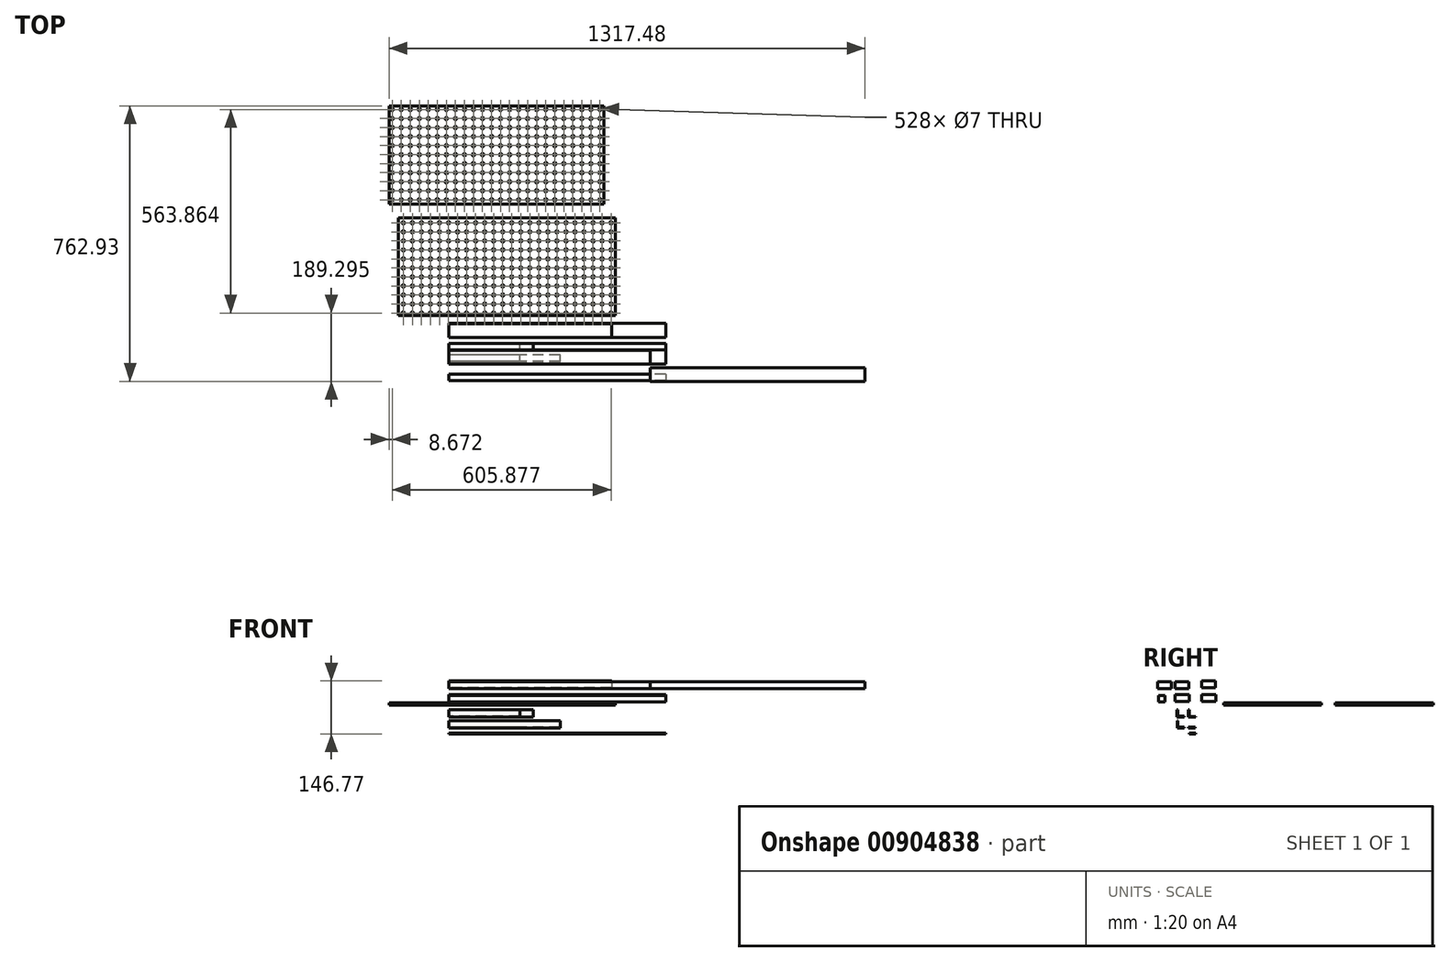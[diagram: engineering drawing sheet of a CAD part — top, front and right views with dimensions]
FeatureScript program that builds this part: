
annotation { "Feature Type Name" : "Feature", "Feature Type Description" : "" }
export const myFeature = defineFeature(function(context is Context, id is Id, definition is map)
    precondition{}
    {
        {
            var Q0;
            Q0=qCreatedBy(makeId("Right.planeOp"),FACE);
            var sketch = newSketch(context, id + "F0", { "sketchPlane" : qUnion([Q0])});
            skLineSegment(sketch, "E0.bottom", {"start": v(-24.33, 9.4) * mm, "end": v(-64.33, 9.4) * mm});
            skLineSegment(sketch, "E0.top", {"start": v(-24.33, 29.4) * mm, "end": v(-64.33, 29.4) * mm});
            skLineSegment(sketch, "E0.left", {"start": v(-24.33, 9.4) * mm, "end": v(-24.33, 29.4) * mm});
            skLineSegment(sketch, "E0.right", {"start": v(-64.33, 9.4) * mm, "end": v(-64.33, 29.4) * mm});
            skPoint(sketch, "E0.middle", {"position": v(-44.33, 19.4) * mm});
            skSolve(sketch);
        }
        {
            var Q0;
            Q0=qCreatedBy(makeId("Right.planeOp"),FACE);
            var sketch = newSketch(context, id + "F1", { "sketchPlane" : qUnion([Q0])});
            skLineSegment(sketch, "E1.bottom", {"start": v(49.06, 9.14) * mm, "end": v(9.06, 9.14) * mm});
            skLineSegment(sketch, "E1.top", {"start": v(49.06, 29.14) * mm, "end": v(9.06, 29.14) * mm});
            skLineSegment(sketch, "E1.left", {"start": v(49.06, 9.14) * mm, "end": v(49.06, 29.14) * mm});
            skLineSegment(sketch, "E1.right", {"start": v(9.06, 9.14) * mm, "end": v(9.06, 29.14) * mm});
            skPoint(sketch, "E1.middle", {"position": v(29.06, 19.14) * mm});
            skSolve(sketch);
        }
        {
            var Q0;
            Q0=qCreatedBy(makeId("Right.planeOp"),FACE);
            var sketch = newSketch(context, id + "F2", { "sketchPlane" : qUnion([Q0])});
            skLineSegment(sketch, "E2", {"start": v(-58.64, -13.36) * mm, "end": v(-58.64, -33.36) * mm});
            skLineSegment(sketch, "E3", {"start": v(-58.64, -33.36) * mm, "end": v(-38.64, -33.36) * mm});
            skLineSegment(sketch, "E4.0", {"start": v(-56.64, -31.36) * mm, "end": v(-38.64, -31.36) * mm});
            skLineSegment(sketch, "E4.1", {"start": v(-56.64, -13.36) * mm, "end": v(-56.64, -31.36) * mm});
            skLineSegment(sketch, "E5", {"start": v(-58.64, -13.36) * mm, "end": v(-56.64, -13.36) * mm});
            skLineSegment(sketch, "E6", {"start": v(-38.64, -31.36) * mm, "end": v(-38.64, -33.36) * mm});
            skSolve(sketch);
        }
        {
            var Q0;
            Q0=qCreatedBy(makeId("Right.planeOp"),FACE);
            var sketch = newSketch(context, id + "F3", { "sketchPlane" : qUnion([Q0])});
            skLineSegment(sketch, "E7.bottom", {"start": v(-91.9, 7.9) * mm, "end": v(-109.9, 7.9) * mm});
            skLineSegment(sketch, "E7.top", {"start": v(-91.9, 25.9) * mm, "end": v(-109.9, 25.9) * mm});
            skLineSegment(sketch, "E7.left", {"start": v(-91.9, 7.9) * mm, "end": v(-91.9, 25.9) * mm});
            skLineSegment(sketch, "E7.right", {"start": v(-109.9, 7.9) * mm, "end": v(-109.9, 25.9) * mm});
            skPoint(sketch, "E7.middle", {"position": v(-100.9, 16.9) * mm});
            skSolve(sketch);
        }
        {
            var Q0;
            Q0=makeQuery(id+"F2.imprint","IMPRINT",FACE,{"disambiguationData":[TD([[makeQuery(id+"F2.imprint","IMPRINT",EDGE,{"derivedFrom":sQuery(id+"F2.wireOp",EDGE,"E2")}),1.0]])]});
            extrude(context, id + "F4", {"entities" : qUnion([Q0]), "depth" : 196.11 * mm, "offsetDistance" : 25.4 * mm});
        }
        {
            var Q0;
            Q0=makeQuery(id+"F1.imprint","IMPRINT",FACE,{"disambiguationData":[TD([[makeQuery(id+"F1.imprint","IMPRINT",EDGE,{"derivedFrom":sQuery(id+"F1.wireOp",EDGE,"E1.bottom")}),-1.0]])]});
            extrude(context, id + "F5", {"entities" : qUnion([Q0]), "depth" : 600 * mm, "offsetDistance" : 25.4 * mm});
        }
        {
            var Q0;
            Q0=makeQuery(id+"F0.imprint","IMPRINT",FACE,{"disambiguationData":[TD([[makeQuery(id+"F0.imprint","IMPRINT",EDGE,{"derivedFrom":sQuery(id+"F0.wireOp",EDGE,"E0.bottom")}),-1.0]])]});
            extrude(context, id + "F6", {"entities" : qUnion([Q0]), "depth" : 600 * mm, "offsetDistance" : 25.4 * mm});
        }
        {
            var Q0;
            Q0=makeQuery(id+"F3.imprint","IMPRINT",FACE,{"disambiguationData":[TD([[makeQuery(id+"F3.imprint","IMPRINT",EDGE,{"derivedFrom":sQuery(id+"F3.wireOp",EDGE,"E7.bottom")}),-1.0]])]});
            extrude(context, id + "F7", {"entities" : qUnion([Q0]), "depth" : 600 * mm, "offsetDistance" : 25.4 * mm});
        }
        {
            var Q0;
            Q0=qCreatedBy(makeId("Right.planeOp"),FACE);
            var sketch = newSketch(context, id + "F8", { "sketchPlane" : qUnion([Q0])});
            skLineSegment(sketch, "E8", {"start": v(-58.2, -43.86) * mm, "end": v(-58.2, -63.86) * mm});
            skLineSegment(sketch, "E9", {"start": v(-58.2, -63.86) * mm, "end": v(-38.2, -63.86) * mm});
            skLineSegment(sketch, "E10.0", {"start": v(-56.2, -61.86) * mm, "end": v(-38.2, -61.86) * mm});
            skLineSegment(sketch, "E10.1", {"start": v(-56.2, -43.86) * mm, "end": v(-56.2, -61.86) * mm});
            skLineSegment(sketch, "E11", {"start": v(-58.2, -43.86) * mm, "end": v(-56.2, -43.86) * mm});
            skLineSegment(sketch, "E12", {"start": v(-38.2, -61.86) * mm, "end": v(-38.2, -63.86) * mm});
            skSolve(sketch);
        }
        {
            var Q0;
            Q0=qSketchRegion(id+"F8",true);
            extrude(context, id + "F9", {"entities" : qUnion([Q0]), "depth" : 308 * mm, "offsetDistance" : 25.4 * mm});
        }
        {
            var Q0;
            Q0=qCreatedBy(makeId("Right.planeOp"),FACE);
            var sketch = newSketch(context, id + "F10", { "sketchPlane" : qUnion([Q0])});
            skLineSegment(sketch, "E13", {"start": v(-26.75, -13.52) * mm, "end": v(-26.75, -33.52) * mm});
            skLineSegment(sketch, "E14", {"start": v(-26.75, -33.52) * mm, "end": v(-6.75, -33.52) * mm});
            skLineSegment(sketch, "E15.0", {"start": v(-24.75, -31.52) * mm, "end": v(-6.75, -31.52) * mm});
            skLineSegment(sketch, "E15.1", {"start": v(-24.75, -13.52) * mm, "end": v(-24.75, -31.52) * mm});
            skLineSegment(sketch, "E16", {"start": v(-26.75, -13.52) * mm, "end": v(-24.75, -13.52) * mm});
            skLineSegment(sketch, "E17", {"start": v(-6.75, -31.52) * mm, "end": v(-6.75, -33.52) * mm});
            skSolve(sketch);
        }
        {
            var Q0;
            Q0=qSketchRegion(id+"F10",true);
            extrude(context, id + "F11", {"entities" : qUnion([Q0]), "depth" : 234 * mm, "offsetDistance" : 25 * mm});
        }
        {
            var Q0;
            Q0=qCreatedBy(makeId("Top.planeOp"),FACE);
            var sketch = newSketch(context, id + "F12", { "sketchPlane" : qUnion([Q0])});
            skLineSegment(sketch, "E18.bottom", {"start": v(-139.49, 340.67) * mm, "end": v(460.51, 340.67) * mm});
            skLineSegment(sketch, "E18.top", {"start": v(-139.49, 70.67) * mm, "end": v(460.51, 70.67) * mm});
            skLineSegment(sketch, "E18.left", {"start": v(-139.49, 340.67) * mm, "end": v(-139.49, 70.67) * mm});
            skLineSegment(sketch, "E18.right", {"start": v(460.51, 340.67) * mm, "end": v(460.51, 70.67) * mm});
            skCircle(sketch, "E19", {"center": v(-126.03, 327.27) * mm, "radius": 3.5 * mm});
            skCircle(sketch, "E20.0.1.0", {"center": v(-126.03, 302.27) * mm, "radius": 3.5 * mm});
            skCircle(sketch, "E20.0.2.0", {"center": v(-126.03, 277.27) * mm, "radius": 3.5 * mm});
            skCircle(sketch, "E20.0.3.0", {"center": v(-126.03, 252.27) * mm, "radius": 3.5 * mm});
            skCircle(sketch, "E20.0.4.0", {"center": v(-126.03, 227.27) * mm, "radius": 3.5 * mm});
            skCircle(sketch, "E20.0.5.0", {"center": v(-126.03, 202.27) * mm, "radius": 3.5 * mm});
            skCircle(sketch, "E20.0.6.0", {"center": v(-126.03, 177.27) * mm, "radius": 3.5 * mm});
            skCircle(sketch, "E20.0.7.0", {"center": v(-126.03, 152.27) * mm, "radius": 3.5 * mm});
            skCircle(sketch, "E20.0.8.0", {"center": v(-126.03, 127.27) * mm, "radius": 3.5 * mm});
            skCircle(sketch, "E20.0.9.0", {"center": v(-126.03, 102.27) * mm, "radius": 3.5 * mm});
            skCircle(sketch, "E20.0.10.0", {"center": v(-126.03, 77.27) * mm, "radius": 3.5 * mm});
            skCircle(sketch, "E20.1.0.0", {"center": v(-101.03, 327.27) * mm, "radius": 3.5 * mm});
            skCircle(sketch, "E20.1.1.0", {"center": v(-101.03, 302.27) * mm, "radius": 3.5 * mm});
            skCircle(sketch, "E20.1.2.0", {"center": v(-101.03, 277.27) * mm, "radius": 3.5 * mm});
            skCircle(sketch, "E20.1.3.0", {"center": v(-101.03, 252.27) * mm, "radius": 3.5 * mm});
            skCircle(sketch, "E20.1.4.0", {"center": v(-101.03, 227.27) * mm, "radius": 3.5 * mm});
            skCircle(sketch, "E20.1.5.0", {"center": v(-101.03, 202.27) * mm, "radius": 3.5 * mm});
            skCircle(sketch, "E20.1.6.0", {"center": v(-101.03, 177.27) * mm, "radius": 3.5 * mm});
            skCircle(sketch, "E20.1.7.0", {"center": v(-101.03, 152.27) * mm, "radius": 3.5 * mm});
            skCircle(sketch, "E20.1.8.0", {"center": v(-101.03, 127.27) * mm, "radius": 3.5 * mm});
            skCircle(sketch, "E20.1.9.0", {"center": v(-101.03, 102.27) * mm, "radius": 3.5 * mm});
            skCircle(sketch, "E20.1.10.0", {"center": v(-101.03, 77.27) * mm, "radius": 3.5 * mm});
            skCircle(sketch, "E20.2.0.0", {"center": v(-76.03, 327.27) * mm, "radius": 3.5 * mm});
            skCircle(sketch, "E20.2.1.0", {"center": v(-76.03, 302.27) * mm, "radius": 3.5 * mm});
            skCircle(sketch, "E20.2.2.0", {"center": v(-76.03, 277.27) * mm, "radius": 3.5 * mm});
            skCircle(sketch, "E20.2.3.0", {"center": v(-76.03, 252.27) * mm, "radius": 3.5 * mm});
            skCircle(sketch, "E20.2.4.0", {"center": v(-76.03, 227.27) * mm, "radius": 3.5 * mm});
            skCircle(sketch, "E20.2.5.0", {"center": v(-76.03, 202.27) * mm, "radius": 3.5 * mm});
            skCircle(sketch, "E20.2.6.0", {"center": v(-76.03, 177.27) * mm, "radius": 3.5 * mm});
            skCircle(sketch, "E20.2.7.0", {"center": v(-76.03, 152.27) * mm, "radius": 3.5 * mm});
            skCircle(sketch, "E20.2.8.0", {"center": v(-76.03, 127.27) * mm, "radius": 3.5 * mm});
            skCircle(sketch, "E20.2.9.0", {"center": v(-76.03, 102.27) * mm, "radius": 3.5 * mm});
            skCircle(sketch, "E20.2.10.0", {"center": v(-76.03, 77.27) * mm, "radius": 3.5 * mm});
            skCircle(sketch, "E20.3.0.0", {"center": v(-51.03, 327.27) * mm, "radius": 3.5 * mm});
            skCircle(sketch, "E20.3.1.0", {"center": v(-51.03, 302.27) * mm, "radius": 3.5 * mm});
            skCircle(sketch, "E20.3.2.0", {"center": v(-51.03, 277.27) * mm, "radius": 3.5 * mm});
            skCircle(sketch, "E20.3.3.0", {"center": v(-51.03, 252.27) * mm, "radius": 3.5 * mm});
            skCircle(sketch, "E20.3.4.0", {"center": v(-51.03, 227.27) * mm, "radius": 3.5 * mm});
            skCircle(sketch, "E20.3.5.0", {"center": v(-51.03, 202.27) * mm, "radius": 3.5 * mm});
            skCircle(sketch, "E20.3.6.0", {"center": v(-51.03, 177.27) * mm, "radius": 3.5 * mm});
            skCircle(sketch, "E20.3.7.0", {"center": v(-51.03, 152.27) * mm, "radius": 3.5 * mm});
            skCircle(sketch, "E20.3.8.0", {"center": v(-51.03, 127.27) * mm, "radius": 3.5 * mm});
            skCircle(sketch, "E20.3.9.0", {"center": v(-51.03, 102.27) * mm, "radius": 3.5 * mm});
            skCircle(sketch, "E20.3.10.0", {"center": v(-51.03, 77.27) * mm, "radius": 3.5 * mm});
            skCircle(sketch, "E20.4.0.0", {"center": v(-26.03, 327.27) * mm, "radius": 3.5 * mm});
            skCircle(sketch, "E20.4.1.0", {"center": v(-26.03, 302.27) * mm, "radius": 3.5 * mm});
            skCircle(sketch, "E20.4.2.0", {"center": v(-26.03, 277.27) * mm, "radius": 3.5 * mm});
            skCircle(sketch, "E20.4.3.0", {"center": v(-26.03, 252.27) * mm, "radius": 3.5 * mm});
            skCircle(sketch, "E20.4.4.0", {"center": v(-26.03, 227.27) * mm, "radius": 3.5 * mm});
            skCircle(sketch, "E20.4.5.0", {"center": v(-26.03, 202.27) * mm, "radius": 3.5 * mm});
            skCircle(sketch, "E20.4.6.0", {"center": v(-26.03, 177.27) * mm, "radius": 3.5 * mm});
            skCircle(sketch, "E20.4.7.0", {"center": v(-26.03, 152.27) * mm, "radius": 3.5 * mm});
            skCircle(sketch, "E20.4.8.0", {"center": v(-26.03, 127.27) * mm, "radius": 3.5 * mm});
            skCircle(sketch, "E20.4.9.0", {"center": v(-26.03, 102.27) * mm, "radius": 3.5 * mm});
            skCircle(sketch, "E20.4.10.0", {"center": v(-26.03, 77.27) * mm, "radius": 3.5 * mm});
            skCircle(sketch, "E20.5.0.0", {"center": v(-1.03, 327.27) * mm, "radius": 3.5 * mm});
            skCircle(sketch, "E20.5.1.0", {"center": v(-1.03, 302.27) * mm, "radius": 3.5 * mm});
            skCircle(sketch, "E20.5.2.0", {"center": v(-1.03, 277.27) * mm, "radius": 3.5 * mm});
            skCircle(sketch, "E20.5.3.0", {"center": v(-1.03, 252.27) * mm, "radius": 3.5 * mm});
            skCircle(sketch, "E20.5.4.0", {"center": v(-1.03, 227.27) * mm, "radius": 3.5 * mm});
            skCircle(sketch, "E20.5.5.0", {"center": v(-1.03, 202.27) * mm, "radius": 3.5 * mm});
            skCircle(sketch, "E20.5.6.0", {"center": v(-1.03, 177.27) * mm, "radius": 3.5 * mm});
            skCircle(sketch, "E20.5.7.0", {"center": v(-1.03, 152.27) * mm, "radius": 3.5 * mm});
            skCircle(sketch, "E20.5.8.0", {"center": v(-1.03, 127.27) * mm, "radius": 3.5 * mm});
            skCircle(sketch, "E20.5.9.0", {"center": v(-1.03, 102.27) * mm, "radius": 3.5 * mm});
            skCircle(sketch, "E20.5.10.0", {"center": v(-1.03, 77.27) * mm, "radius": 3.5 * mm});
            skCircle(sketch, "E20.6.0.0", {"center": v(23.97, 327.27) * mm, "radius": 3.5 * mm});
            skCircle(sketch, "E20.6.1.0", {"center": v(23.97, 302.27) * mm, "radius": 3.5 * mm});
            skCircle(sketch, "E20.6.2.0", {"center": v(23.97, 277.27) * mm, "radius": 3.5 * mm});
            skCircle(sketch, "E20.6.3.0", {"center": v(23.97, 252.27) * mm, "radius": 3.5 * mm});
            skCircle(sketch, "E20.6.4.0", {"center": v(23.97, 227.27) * mm, "radius": 3.5 * mm});
            skCircle(sketch, "E20.6.5.0", {"center": v(23.97, 202.27) * mm, "radius": 3.5 * mm});
            skCircle(sketch, "E20.6.6.0", {"center": v(23.97, 177.27) * mm, "radius": 3.5 * mm});
            skCircle(sketch, "E20.6.7.0", {"center": v(23.97, 152.27) * mm, "radius": 3.5 * mm});
            skCircle(sketch, "E20.6.8.0", {"center": v(23.97, 127.27) * mm, "radius": 3.5 * mm});
            skCircle(sketch, "E20.6.9.0", {"center": v(23.97, 102.27) * mm, "radius": 3.5 * mm});
            skCircle(sketch, "E20.6.10.0", {"center": v(23.97, 77.27) * mm, "radius": 3.5 * mm});
            skCircle(sketch, "E20.7.0.0", {"center": v(48.97, 327.27) * mm, "radius": 3.5 * mm});
            skCircle(sketch, "E20.7.1.0", {"center": v(48.97, 302.27) * mm, "radius": 3.5 * mm});
            skCircle(sketch, "E20.7.2.0", {"center": v(48.97, 277.27) * mm, "radius": 3.5 * mm});
            skCircle(sketch, "E20.7.3.0", {"center": v(48.97, 252.27) * mm, "radius": 3.5 * mm});
            skCircle(sketch, "E20.7.4.0", {"center": v(48.97, 227.27) * mm, "radius": 3.5 * mm});
            skCircle(sketch, "E20.7.5.0", {"center": v(48.97, 202.27) * mm, "radius": 3.5 * mm});
            skCircle(sketch, "E20.7.6.0", {"center": v(48.97, 177.27) * mm, "radius": 3.5 * mm});
            skCircle(sketch, "E20.7.7.0", {"center": v(48.97, 152.27) * mm, "radius": 3.5 * mm});
            skCircle(sketch, "E20.7.8.0", {"center": v(48.97, 127.27) * mm, "radius": 3.5 * mm});
            skCircle(sketch, "E20.7.9.0", {"center": v(48.97, 102.27) * mm, "radius": 3.5 * mm});
            skCircle(sketch, "E20.7.10.0", {"center": v(48.97, 77.27) * mm, "radius": 3.5 * mm});
            skCircle(sketch, "E20.8.0.0", {"center": v(73.97, 327.27) * mm, "radius": 3.5 * mm});
            skCircle(sketch, "E20.8.1.0", {"center": v(73.97, 302.27) * mm, "radius": 3.5 * mm});
            skCircle(sketch, "E20.8.2.0", {"center": v(73.97, 277.27) * mm, "radius": 3.5 * mm});
            skCircle(sketch, "E20.8.3.0", {"center": v(73.97, 252.27) * mm, "radius": 3.5 * mm});
            skCircle(sketch, "E20.8.4.0", {"center": v(73.97, 227.27) * mm, "radius": 3.5 * mm});
            skCircle(sketch, "E20.8.5.0", {"center": v(73.97, 202.27) * mm, "radius": 3.5 * mm});
            skCircle(sketch, "E20.8.6.0", {"center": v(73.97, 177.27) * mm, "radius": 3.5 * mm});
            skCircle(sketch, "E20.8.7.0", {"center": v(73.97, 152.27) * mm, "radius": 3.5 * mm});
            skCircle(sketch, "E20.8.8.0", {"center": v(73.97, 127.27) * mm, "radius": 3.5 * mm});
            skCircle(sketch, "E20.8.9.0", {"center": v(73.97, 102.27) * mm, "radius": 3.5 * mm});
            skCircle(sketch, "E20.8.10.0", {"center": v(73.97, 77.27) * mm, "radius": 3.5 * mm});
            skCircle(sketch, "E20.9.0.0", {"center": v(98.97, 327.27) * mm, "radius": 3.5 * mm});
            skCircle(sketch, "E20.9.1.0", {"center": v(98.97, 302.27) * mm, "radius": 3.5 * mm});
            skCircle(sketch, "E20.9.2.0", {"center": v(98.97, 277.27) * mm, "radius": 3.5 * mm});
            skCircle(sketch, "E20.9.3.0", {"center": v(98.97, 252.27) * mm, "radius": 3.5 * mm});
            skCircle(sketch, "E20.9.4.0", {"center": v(98.97, 227.27) * mm, "radius": 3.5 * mm});
            skCircle(sketch, "E20.9.5.0", {"center": v(98.97, 202.27) * mm, "radius": 3.5 * mm});
            skCircle(sketch, "E20.9.6.0", {"center": v(98.97, 177.27) * mm, "radius": 3.5 * mm});
            skCircle(sketch, "E20.9.7.0", {"center": v(98.97, 152.27) * mm, "radius": 3.5 * mm});
            skCircle(sketch, "E20.9.8.0", {"center": v(98.97, 127.27) * mm, "radius": 3.5 * mm});
            skCircle(sketch, "E20.9.9.0", {"center": v(98.97, 102.27) * mm, "radius": 3.5 * mm});
            skCircle(sketch, "E20.9.10.0", {"center": v(98.97, 77.27) * mm, "radius": 3.5 * mm});
            skCircle(sketch, "E20.10.0.0", {"center": v(123.97, 327.27) * mm, "radius": 3.5 * mm});
            skCircle(sketch, "E20.10.1.0", {"center": v(123.97, 302.27) * mm, "radius": 3.5 * mm});
            skCircle(sketch, "E20.10.2.0", {"center": v(123.97, 277.27) * mm, "radius": 3.5 * mm});
            skCircle(sketch, "E20.10.3.0", {"center": v(123.97, 252.27) * mm, "radius": 3.5 * mm});
            skCircle(sketch, "E20.10.4.0", {"center": v(123.97, 227.27) * mm, "radius": 3.5 * mm});
            skCircle(sketch, "E20.10.5.0", {"center": v(123.97, 202.27) * mm, "radius": 3.5 * mm});
            skCircle(sketch, "E20.10.6.0", {"center": v(123.97, 177.27) * mm, "radius": 3.5 * mm});
            skCircle(sketch, "E20.10.7.0", {"center": v(123.97, 152.27) * mm, "radius": 3.5 * mm});
            skCircle(sketch, "E20.10.8.0", {"center": v(123.97, 127.27) * mm, "radius": 3.5 * mm});
            skCircle(sketch, "E20.10.9.0", {"center": v(123.97, 102.27) * mm, "radius": 3.5 * mm});
            skCircle(sketch, "E20.10.10.0", {"center": v(123.97, 77.27) * mm, "radius": 3.5 * mm});
            skCircle(sketch, "E20.11.0.0", {"center": v(148.97, 327.27) * mm, "radius": 3.5 * mm});
            skCircle(sketch, "E20.11.1.0", {"center": v(148.97, 302.27) * mm, "radius": 3.5 * mm});
            skCircle(sketch, "E20.11.2.0", {"center": v(148.97, 277.27) * mm, "radius": 3.5 * mm});
            skCircle(sketch, "E20.11.3.0", {"center": v(148.97, 252.27) * mm, "radius": 3.5 * mm});
            skCircle(sketch, "E20.11.4.0", {"center": v(148.97, 227.27) * mm, "radius": 3.5 * mm});
            skCircle(sketch, "E20.11.5.0", {"center": v(148.97, 202.27) * mm, "radius": 3.5 * mm});
            skCircle(sketch, "E20.11.6.0", {"center": v(148.97, 177.27) * mm, "radius": 3.5 * mm});
            skCircle(sketch, "E20.11.7.0", {"center": v(148.97, 152.27) * mm, "radius": 3.5 * mm});
            skCircle(sketch, "E20.11.8.0", {"center": v(148.97, 127.27) * mm, "radius": 3.5 * mm});
            skCircle(sketch, "E20.11.9.0", {"center": v(148.97, 102.27) * mm, "radius": 3.5 * mm});
            skCircle(sketch, "E20.11.10.0", {"center": v(148.97, 77.27) * mm, "radius": 3.5 * mm});
            skCircle(sketch, "E20.12.0.0", {"center": v(173.97, 327.27) * mm, "radius": 3.5 * mm});
            skCircle(sketch, "E20.12.1.0", {"center": v(173.97, 302.27) * mm, "radius": 3.5 * mm});
            skCircle(sketch, "E20.12.2.0", {"center": v(173.97, 277.27) * mm, "radius": 3.5 * mm});
            skCircle(sketch, "E20.12.3.0", {"center": v(173.97, 252.27) * mm, "radius": 3.5 * mm});
            skCircle(sketch, "E20.12.4.0", {"center": v(173.97, 227.27) * mm, "radius": 3.5 * mm});
            skCircle(sketch, "E20.12.5.0", {"center": v(173.97, 202.27) * mm, "radius": 3.5 * mm});
            skCircle(sketch, "E20.12.6.0", {"center": v(173.97, 177.27) * mm, "radius": 3.5 * mm});
            skCircle(sketch, "E20.12.7.0", {"center": v(173.97, 152.27) * mm, "radius": 3.5 * mm});
            skCircle(sketch, "E20.12.8.0", {"center": v(173.97, 127.27) * mm, "radius": 3.5 * mm});
            skCircle(sketch, "E20.12.9.0", {"center": v(173.97, 102.27) * mm, "radius": 3.5 * mm});
            skCircle(sketch, "E20.12.10.0", {"center": v(173.97, 77.27) * mm, "radius": 3.5 * mm});
            skCircle(sketch, "E20.13.0.0", {"center": v(198.97, 327.27) * mm, "radius": 3.5 * mm});
            skCircle(sketch, "E20.13.1.0", {"center": v(198.97, 302.27) * mm, "radius": 3.5 * mm});
            skCircle(sketch, "E20.13.2.0", {"center": v(198.97, 277.27) * mm, "radius": 3.5 * mm});
            skCircle(sketch, "E20.13.3.0", {"center": v(198.97, 252.27) * mm, "radius": 3.5 * mm});
            skCircle(sketch, "E20.13.4.0", {"center": v(198.97, 227.27) * mm, "radius": 3.5 * mm});
            skCircle(sketch, "E20.13.5.0", {"center": v(198.97, 202.27) * mm, "radius": 3.5 * mm});
            skCircle(sketch, "E20.13.6.0", {"center": v(198.97, 177.27) * mm, "radius": 3.5 * mm});
            skCircle(sketch, "E20.13.7.0", {"center": v(198.97, 152.27) * mm, "radius": 3.5 * mm});
            skCircle(sketch, "E20.13.8.0", {"center": v(198.97, 127.27) * mm, "radius": 3.5 * mm});
            skCircle(sketch, "E20.13.9.0", {"center": v(198.97, 102.27) * mm, "radius": 3.5 * mm});
            skCircle(sketch, "E20.13.10.0", {"center": v(198.97, 77.27) * mm, "radius": 3.5 * mm});
            skCircle(sketch, "E20.14.0.0", {"center": v(223.97, 327.27) * mm, "radius": 3.5 * mm});
            skCircle(sketch, "E20.14.1.0", {"center": v(223.97, 302.27) * mm, "radius": 3.5 * mm});
            skCircle(sketch, "E20.14.2.0", {"center": v(223.97, 277.27) * mm, "radius": 3.5 * mm});
            skCircle(sketch, "E20.14.3.0", {"center": v(223.97, 252.27) * mm, "radius": 3.5 * mm});
            skCircle(sketch, "E20.14.4.0", {"center": v(223.97, 227.27) * mm, "radius": 3.5 * mm});
            skCircle(sketch, "E20.14.5.0", {"center": v(223.97, 202.27) * mm, "radius": 3.5 * mm});
            skCircle(sketch, "E20.14.6.0", {"center": v(223.97, 177.27) * mm, "radius": 3.5 * mm});
            skCircle(sketch, "E20.14.7.0", {"center": v(223.97, 152.27) * mm, "radius": 3.5 * mm});
            skCircle(sketch, "E20.14.8.0", {"center": v(223.97, 127.27) * mm, "radius": 3.5 * mm});
            skCircle(sketch, "E20.14.9.0", {"center": v(223.97, 102.27) * mm, "radius": 3.5 * mm});
            skCircle(sketch, "E20.14.10.0", {"center": v(223.97, 77.27) * mm, "radius": 3.5 * mm});
            skCircle(sketch, "E20.15.0.0", {"center": v(248.97, 327.27) * mm, "radius": 3.5 * mm});
            skCircle(sketch, "E20.15.1.0", {"center": v(248.97, 302.27) * mm, "radius": 3.5 * mm});
            skCircle(sketch, "E20.15.2.0", {"center": v(248.97, 277.27) * mm, "radius": 3.5 * mm});
            skCircle(sketch, "E20.15.3.0", {"center": v(248.97, 252.27) * mm, "radius": 3.5 * mm});
            skCircle(sketch, "E20.15.4.0", {"center": v(248.97, 227.27) * mm, "radius": 3.5 * mm});
            skCircle(sketch, "E20.15.5.0", {"center": v(248.97, 202.27) * mm, "radius": 3.5 * mm});
            skCircle(sketch, "E20.15.6.0", {"center": v(248.97, 177.27) * mm, "radius": 3.5 * mm});
            skCircle(sketch, "E20.15.7.0", {"center": v(248.97, 152.27) * mm, "radius": 3.5 * mm});
            skCircle(sketch, "E20.15.8.0", {"center": v(248.97, 127.27) * mm, "radius": 3.5 * mm});
            skCircle(sketch, "E20.15.9.0", {"center": v(248.97, 102.27) * mm, "radius": 3.5 * mm});
            skCircle(sketch, "E20.15.10.0", {"center": v(248.97, 77.27) * mm, "radius": 3.5 * mm});
            skCircle(sketch, "E20.16.0.0", {"center": v(273.97, 327.27) * mm, "radius": 3.5 * mm});
            skCircle(sketch, "E20.16.1.0", {"center": v(273.97, 302.27) * mm, "radius": 3.5 * mm});
            skCircle(sketch, "E20.16.2.0", {"center": v(273.97, 277.27) * mm, "radius": 3.5 * mm});
            skCircle(sketch, "E20.16.3.0", {"center": v(273.97, 252.27) * mm, "radius": 3.5 * mm});
            skCircle(sketch, "E20.16.4.0", {"center": v(273.97, 227.27) * mm, "radius": 3.5 * mm});
            skCircle(sketch, "E20.16.5.0", {"center": v(273.97, 202.27) * mm, "radius": 3.5 * mm});
            skCircle(sketch, "E20.16.6.0", {"center": v(273.97, 177.27) * mm, "radius": 3.5 * mm});
            skCircle(sketch, "E20.16.7.0", {"center": v(273.97, 152.27) * mm, "radius": 3.5 * mm});
            skCircle(sketch, "E20.16.8.0", {"center": v(273.97, 127.27) * mm, "radius": 3.5 * mm});
            skCircle(sketch, "E20.16.9.0", {"center": v(273.97, 102.27) * mm, "radius": 3.5 * mm});
            skCircle(sketch, "E20.16.10.0", {"center": v(273.97, 77.27) * mm, "radius": 3.5 * mm});
            skCircle(sketch, "E20.17.0.0", {"center": v(298.97, 327.27) * mm, "radius": 3.5 * mm});
            skCircle(sketch, "E20.17.1.0", {"center": v(298.97, 302.27) * mm, "radius": 3.5 * mm});
            skCircle(sketch, "E20.17.2.0", {"center": v(298.97, 277.27) * mm, "radius": 3.5 * mm});
            skCircle(sketch, "E20.17.3.0", {"center": v(298.97, 252.27) * mm, "radius": 3.5 * mm});
            skCircle(sketch, "E20.17.4.0", {"center": v(298.97, 227.27) * mm, "radius": 3.5 * mm});
            skCircle(sketch, "E20.17.5.0", {"center": v(298.97, 202.27) * mm, "radius": 3.5 * mm});
            skCircle(sketch, "E20.17.6.0", {"center": v(298.97, 177.27) * mm, "radius": 3.5 * mm});
            skCircle(sketch, "E20.17.7.0", {"center": v(298.97, 152.27) * mm, "radius": 3.5 * mm});
            skCircle(sketch, "E20.17.8.0", {"center": v(298.97, 127.27) * mm, "radius": 3.5 * mm});
            skCircle(sketch, "E20.17.9.0", {"center": v(298.97, 102.27) * mm, "radius": 3.5 * mm});
            skCircle(sketch, "E20.17.10.0", {"center": v(298.97, 77.27) * mm, "radius": 3.5 * mm});
            skCircle(sketch, "E20.18.0.0", {"center": v(323.97, 327.27) * mm, "radius": 3.5 * mm});
            skCircle(sketch, "E20.18.1.0", {"center": v(323.97, 302.27) * mm, "radius": 3.5 * mm});
            skCircle(sketch, "E20.18.2.0", {"center": v(323.97, 277.27) * mm, "radius": 3.5 * mm});
            skCircle(sketch, "E20.18.3.0", {"center": v(323.97, 252.27) * mm, "radius": 3.5 * mm});
            skCircle(sketch, "E20.18.4.0", {"center": v(323.97, 227.27) * mm, "radius": 3.5 * mm});
            skCircle(sketch, "E20.18.5.0", {"center": v(323.97, 202.27) * mm, "radius": 3.5 * mm});
            skCircle(sketch, "E20.18.6.0", {"center": v(323.97, 177.27) * mm, "radius": 3.5 * mm});
            skCircle(sketch, "E20.18.7.0", {"center": v(323.97, 152.27) * mm, "radius": 3.5 * mm});
            skCircle(sketch, "E20.18.8.0", {"center": v(323.97, 127.27) * mm, "radius": 3.5 * mm});
            skCircle(sketch, "E20.18.9.0", {"center": v(323.97, 102.27) * mm, "radius": 3.5 * mm});
            skCircle(sketch, "E20.18.10.0", {"center": v(323.97, 77.27) * mm, "radius": 3.5 * mm});
            skCircle(sketch, "E20.19.0.0", {"center": v(348.97, 327.27) * mm, "radius": 3.5 * mm});
            skCircle(sketch, "E20.19.1.0", {"center": v(348.97, 302.27) * mm, "radius": 3.5 * mm});
            skCircle(sketch, "E20.19.2.0", {"center": v(348.97, 277.27) * mm, "radius": 3.5 * mm});
            skCircle(sketch, "E20.19.3.0", {"center": v(348.97, 252.27) * mm, "radius": 3.5 * mm});
            skCircle(sketch, "E20.19.4.0", {"center": v(348.97, 227.27) * mm, "radius": 3.5 * mm});
            skCircle(sketch, "E20.19.5.0", {"center": v(348.97, 202.27) * mm, "radius": 3.5 * mm});
            skCircle(sketch, "E20.19.6.0", {"center": v(348.97, 177.27) * mm, "radius": 3.5 * mm});
            skCircle(sketch, "E20.19.7.0", {"center": v(348.97, 152.27) * mm, "radius": 3.5 * mm});
            skCircle(sketch, "E20.19.8.0", {"center": v(348.97, 127.27) * mm, "radius": 3.5 * mm});
            skCircle(sketch, "E20.19.9.0", {"center": v(348.97, 102.27) * mm, "radius": 3.5 * mm});
            skCircle(sketch, "E20.19.10.0", {"center": v(348.97, 77.27) * mm, "radius": 3.5 * mm});
            skCircle(sketch, "E20.20.0.0", {"center": v(373.97, 327.27) * mm, "radius": 3.5 * mm});
            skCircle(sketch, "E20.20.1.0", {"center": v(373.97, 302.27) * mm, "radius": 3.5 * mm});
            skCircle(sketch, "E20.20.2.0", {"center": v(373.97, 277.27) * mm, "radius": 3.5 * mm});
            skCircle(sketch, "E20.20.3.0", {"center": v(373.97, 252.27) * mm, "radius": 3.5 * mm});
            skCircle(sketch, "E20.20.4.0", {"center": v(373.97, 227.27) * mm, "radius": 3.5 * mm});
            skCircle(sketch, "E20.20.5.0", {"center": v(373.97, 202.27) * mm, "radius": 3.5 * mm});
            skCircle(sketch, "E20.20.6.0", {"center": v(373.97, 177.27) * mm, "radius": 3.5 * mm});
            skCircle(sketch, "E20.20.7.0", {"center": v(373.97, 152.27) * mm, "radius": 3.5 * mm});
            skCircle(sketch, "E20.20.8.0", {"center": v(373.97, 127.27) * mm, "radius": 3.5 * mm});
            skCircle(sketch, "E20.20.9.0", {"center": v(373.97, 102.27) * mm, "radius": 3.5 * mm});
            skCircle(sketch, "E20.20.10.0", {"center": v(373.97, 77.27) * mm, "radius": 3.5 * mm});
            skCircle(sketch, "E20.21.0.0", {"center": v(398.97, 327.27) * mm, "radius": 3.5 * mm});
            skCircle(sketch, "E20.21.1.0", {"center": v(398.97, 302.27) * mm, "radius": 3.5 * mm});
            skCircle(sketch, "E20.21.2.0", {"center": v(398.97, 277.27) * mm, "radius": 3.5 * mm});
            skCircle(sketch, "E20.21.3.0", {"center": v(398.97, 252.27) * mm, "radius": 3.5 * mm});
            skCircle(sketch, "E20.21.4.0", {"center": v(398.97, 227.27) * mm, "radius": 3.5 * mm});
            skCircle(sketch, "E20.21.5.0", {"center": v(398.97, 202.27) * mm, "radius": 3.5 * mm});
            skCircle(sketch, "E20.21.6.0", {"center": v(398.97, 177.27) * mm, "radius": 3.5 * mm});
            skCircle(sketch, "E20.21.7.0", {"center": v(398.97, 152.27) * mm, "radius": 3.5 * mm});
            skCircle(sketch, "E20.21.8.0", {"center": v(398.97, 127.27) * mm, "radius": 3.5 * mm});
            skCircle(sketch, "E20.21.9.0", {"center": v(398.97, 102.27) * mm, "radius": 3.5 * mm});
            skCircle(sketch, "E20.21.10.0", {"center": v(398.97, 77.27) * mm, "radius": 3.5 * mm});
            skCircle(sketch, "E20.22.0.0", {"center": v(423.97, 327.27) * mm, "radius": 3.5 * mm});
            skCircle(sketch, "E20.22.1.0", {"center": v(423.97, 302.27) * mm, "radius": 3.5 * mm});
            skCircle(sketch, "E20.22.2.0", {"center": v(423.97, 277.27) * mm, "radius": 3.5 * mm});
            skCircle(sketch, "E20.22.3.0", {"center": v(423.97, 252.27) * mm, "radius": 3.5 * mm});
            skCircle(sketch, "E20.22.4.0", {"center": v(423.97, 227.27) * mm, "radius": 3.5 * mm});
            skCircle(sketch, "E20.22.5.0", {"center": v(423.97, 202.27) * mm, "radius": 3.5 * mm});
            skCircle(sketch, "E20.22.6.0", {"center": v(423.97, 177.27) * mm, "radius": 3.5 * mm});
            skCircle(sketch, "E20.22.7.0", {"center": v(423.97, 152.27) * mm, "radius": 3.5 * mm});
            skCircle(sketch, "E20.22.8.0", {"center": v(423.97, 127.27) * mm, "radius": 3.5 * mm});
            skCircle(sketch, "E20.22.9.0", {"center": v(423.97, 102.27) * mm, "radius": 3.5 * mm});
            skCircle(sketch, "E20.22.10.0", {"center": v(423.97, 77.27) * mm, "radius": 3.5 * mm});
            skCircle(sketch, "E20.23.0.0", {"center": v(448.97, 327.27) * mm, "radius": 3.5 * mm});
            skCircle(sketch, "E20.23.1.0", {"center": v(448.97, 302.27) * mm, "radius": 3.5 * mm});
            skCircle(sketch, "E20.23.2.0", {"center": v(448.97, 277.27) * mm, "radius": 3.5 * mm});
            skCircle(sketch, "E20.23.3.0", {"center": v(448.97, 252.27) * mm, "radius": 3.5 * mm});
            skCircle(sketch, "E20.23.4.0", {"center": v(448.97, 227.27) * mm, "radius": 3.5 * mm});
            skCircle(sketch, "E20.23.5.0", {"center": v(448.97, 202.27) * mm, "radius": 3.5 * mm});
            skCircle(sketch, "E20.23.6.0", {"center": v(448.97, 177.27) * mm, "radius": 3.5 * mm});
            skCircle(sketch, "E20.23.7.0", {"center": v(448.97, 152.27) * mm, "radius": 3.5 * mm});
            skCircle(sketch, "E20.23.8.0", {"center": v(448.97, 127.27) * mm, "radius": 3.5 * mm});
            skCircle(sketch, "E20.23.9.0", {"center": v(448.97, 102.27) * mm, "radius": 3.5 * mm});
            skCircle(sketch, "E20.23.10.0", {"center": v(448.97, 77.27) * mm, "radius": 3.5 * mm});
            skLineSegment(sketch, "E20.direction1", {"start": v(-126.03, 327.27) * mm, "end": v(-101.03, 327.27) * mm, "construction": true});
            skLineSegment(sketch, "E20.direction2", {"start": v(-126.03, 327.27) * mm, "end": v(-126.03, 302.27) * mm, "construction": true});
            skSolve(sketch);
        }
        {
            var Q0;
            Q0=qSketchRegion(id+"F12",true);
            extrude(context, id + "F13", {"entities" : qUnion([Q0]), "depth" : 6 * mm, "offsetDistance" : 25 * mm});
        }
        {
            var Q0;
            Q0=qCreatedBy(makeId("Right.planeOp"),FACE);
            var sketch = newSketch(context, id + "F14", { "sketchPlane" : qUnion([Q0])});
            skLineSegment(sketch, "E21.bottom", {"start": v(-26.65, -61.64) * mm, "end": v(-8.65, -61.64) * mm});
            skLineSegment(sketch, "E21.top", {"start": v(-26.65, -63.64) * mm, "end": v(-8.65, -63.64) * mm});
            skLineSegment(sketch, "E21.left", {"start": v(-26.65, -61.64) * mm, "end": v(-26.65, -63.64) * mm});
            skLineSegment(sketch, "E21.right", {"start": v(-8.65, -61.64) * mm, "end": v(-8.65, -63.64) * mm});
            skSolve(sketch);
        }
        {
            var Q0;
            Q0=makeQuery(id+"F14.imprint","IMPRINT",FACE,{"disambiguationData":[TD([[makeQuery(id+"F14.imprint","IMPRINT",EDGE,{"derivedFrom":sQuery(id+"F14.wireOp",EDGE,"E21.bottom")}),-1.0]])]});
            extrude(context, id + "F15", {"entities" : qUnion([Q0]), "depth" : 196.11 * mm, "offsetDistance" : 25 * mm});
        }
        {
            var Q0;
            Q0=qCreatedBy(makeId("Right.planeOp"),FACE);
            var sketch = newSketch(context, id + "F16", { "sketchPlane" : qUnion([Q0])});
            skLineSegment(sketch, "E22.bottom", {"start": v(-25.29, -78.18) * mm, "end": v(-7.29, -78.18) * mm});
            skLineSegment(sketch, "E22.top", {"start": v(-25.29, -80.18) * mm, "end": v(-7.29, -80.18) * mm});
            skLineSegment(sketch, "E22.left", {"start": v(-25.29, -78.18) * mm, "end": v(-25.29, -80.18) * mm});
            skLineSegment(sketch, "E22.right", {"start": v(-7.29, -78.18) * mm, "end": v(-7.29, -80.18) * mm});
            skSolve(sketch);
        }
        {
            var Q0;
            Q0=qSketchRegion(id+"F16",true);
            extrude(context, id + "F17", {"entities" : qUnion([Q0]), "depth" : 600 * mm, "offsetDistance" : 25 * mm});
        }
        {
            var Q0;
            Q0=qCreatedBy(makeId("Right.planeOp"),FACE);
            var sketch = newSketch(context, id + "F18", { "sketchPlane" : qUnion([Q0])});
            skLineSegment(sketch, "E23.bottom", {"start": v(10.1, 66.59) * mm, "end": v(48.2, 66.59) * mm});
            skLineSegment(sketch, "E23.top", {"start": v(10.1, 47.54) * mm, "end": v(48.2, 47.54) * mm});
            skLineSegment(sketch, "E23.left", {"start": v(10.1, 66.59) * mm, "end": v(10.1, 47.54) * mm});
            skLineSegment(sketch, "E23.right", {"start": v(48.2, 66.59) * mm, "end": v(48.2, 47.54) * mm});
            skSolve(sketch);
        }
        {
            var Q0;
            Q0=makeQuery(id+"F18.imprint","IMPRINT",FACE,{"disambiguationData":[TD([[makeQuery(id+"F18.imprint","IMPRINT",EDGE,{"derivedFrom":sQuery(id+"F18.wireOp",EDGE,"E23.bottom")}),-1.0]])]});
            extrude(context, id + "F19", {"entities" : qUnion([Q0]), "depth" : 450 * mm, "offsetDistance" : 25 * mm});
        }
        {
            var Q0;
            Q0=qCreatedBy(makeId("Right.planeOp"),FACE);
            var sketch = newSketch(context, id + "F20", { "sketchPlane" : qUnion([Q0])});
            skLineSegment(sketch, "E24.bottom", {"start": v(-64.16, 64.54) * mm, "end": v(-26.06, 64.54) * mm});
            skLineSegment(sketch, "E24.top", {"start": v(-64.16, 45.49) * mm, "end": v(-26.06, 45.49) * mm});
            skLineSegment(sketch, "E24.left", {"start": v(-64.16, 64.54) * mm, "end": v(-64.16, 45.49) * mm});
            skLineSegment(sketch, "E24.right", {"start": v(-26.06, 64.54) * mm, "end": v(-26.06, 45.49) * mm});
            skSolve(sketch);
        }
        {
            var Q0;
            Q0=makeQuery(id+"F20.imprint","IMPRINT",FACE,{"disambiguationData":[TD([[makeQuery(id+"F20.imprint","IMPRINT",EDGE,{"derivedFrom":sQuery(id+"F20.wireOp",EDGE,"E24.bottom")}),-1.0]])]});
            extrude(context, id + "F21", {"entities" : qUnion([Q0]), "depth" : 556.9 * mm, "offsetDistance" : 25 * mm});
        }
        {
            var Q0;
            Q0=makeQuery(id+"F21.opExtrude","CAP_FACE",FACE,{"disambiguationData":[OSD([sQuery(id+"F20.wireOp",EDGE,"E24.bottom"),sQuery(id+"F20.wireOp",EDGE,"E24.top"),sQuery(id+"F20.wireOp",EDGE,"E24.left"),sQuery(id+"F20.wireOp",EDGE,"E24.right")])],"isStart":false});
            var sketch = newSketch(context, id + "F22", { "sketchPlane" : qUnion([Q0])});
            skLineSegment(sketch, "E25.bottom", {"start": v(-112.02, 64.54) * mm, "end": v(-73.92, 64.54) * mm});
            skLineSegment(sketch, "E25.top", {"start": v(-112.02, 45.49) * mm, "end": v(-73.92, 45.49) * mm});
            skLineSegment(sketch, "E25.left", {"start": v(-112.02, 64.54) * mm, "end": v(-112.02, 45.49) * mm});
            skLineSegment(sketch, "E25.right", {"start": v(-73.92, 64.54) * mm, "end": v(-73.92, 45.49) * mm});
            skSolve(sketch);
        }
        {
            var Q0;
            Q0=makeQuery(id+"F22.imprint","IMPRINT",FACE,{"disambiguationData":[TD([[makeQuery(id+"F22.imprint","IMPRINT",EDGE,{"derivedFrom":sQuery(id+"F22.wireOp",EDGE,"E25.bottom")}),-1.0]])]});
            extrude(context, id + "F23", {"entities" : qUnion([Q0]), "depth" : 595 * mm, "offsetDistance" : 25 * mm});
        }
        {
            var Q0;
            Q0=qCreatedBy(makeId("Top.planeOp"),FACE);
            var sketch = newSketch(context, id + "F24", { "sketchPlane" : qUnion([Q0])});
            skLineSegment(sketch, "E26.bottom", {"start": v(-165.58, 650.9) * mm, "end": v(429.42, 650.9) * mm});
            skLineSegment(sketch, "E26.top", {"start": v(-165.58, 378.9) * mm, "end": v(429.42, 378.9) * mm});
            skLineSegment(sketch, "E26.left", {"start": v(-165.58, 650.9) * mm, "end": v(-165.58, 378.9) * mm});
            skLineSegment(sketch, "E26.right", {"start": v(429.42, 650.9) * mm, "end": v(429.42, 378.9) * mm});
            skCircle(sketch, "E27", {"center": v(-156.9, 641.14) * mm, "radius": 3.5 * mm});
            skCircle(sketch, "E28.0.1.0", {"center": v(-156.9, 616.14) * mm, "radius": 3.5 * mm});
            skCircle(sketch, "E28.0.2.0", {"center": v(-156.9, 591.14) * mm, "radius": 3.5 * mm});
            skCircle(sketch, "E28.0.3.0", {"center": v(-156.9, 566.14) * mm, "radius": 3.5 * mm});
            skCircle(sketch, "E28.0.4.0", {"center": v(-156.9, 541.14) * mm, "radius": 3.5 * mm});
            skCircle(sketch, "E28.0.5.0", {"center": v(-156.9, 516.14) * mm, "radius": 3.5 * mm});
            skCircle(sketch, "E28.0.6.0", {"center": v(-156.9, 491.14) * mm, "radius": 3.5 * mm});
            skCircle(sketch, "E28.0.7.0", {"center": v(-156.9, 466.14) * mm, "radius": 3.5 * mm});
            skCircle(sketch, "E28.0.8.0", {"center": v(-156.9, 441.14) * mm, "radius": 3.5 * mm});
            skCircle(sketch, "E28.0.9.0", {"center": v(-156.9, 416.14) * mm, "radius": 3.5 * mm});
            skCircle(sketch, "E28.0.10.0", {"center": v(-156.9, 391.14) * mm, "radius": 3.5 * mm});
            skCircle(sketch, "E28.1.0.0", {"center": v(-131.9, 641.14) * mm, "radius": 3.5 * mm});
            skCircle(sketch, "E28.1.1.0", {"center": v(-131.9, 616.14) * mm, "radius": 3.5 * mm});
            skCircle(sketch, "E28.1.2.0", {"center": v(-131.9, 591.14) * mm, "radius": 3.5 * mm});
            skCircle(sketch, "E28.1.3.0", {"center": v(-131.9, 566.14) * mm, "radius": 3.5 * mm});
            skCircle(sketch, "E28.1.4.0", {"center": v(-131.9, 541.14) * mm, "radius": 3.5 * mm});
            skCircle(sketch, "E28.1.5.0", {"center": v(-131.9, 516.14) * mm, "radius": 3.5 * mm});
            skCircle(sketch, "E28.1.6.0", {"center": v(-131.9, 491.14) * mm, "radius": 3.5 * mm});
            skCircle(sketch, "E28.1.7.0", {"center": v(-131.9, 466.14) * mm, "radius": 3.5 * mm});
            skCircle(sketch, "E28.1.8.0", {"center": v(-131.9, 441.14) * mm, "radius": 3.5 * mm});
            skCircle(sketch, "E28.1.9.0", {"center": v(-131.9, 416.14) * mm, "radius": 3.5 * mm});
            skCircle(sketch, "E28.1.10.0", {"center": v(-131.9, 391.14) * mm, "radius": 3.5 * mm});
            skCircle(sketch, "E28.2.0.0", {"center": v(-106.9, 641.14) * mm, "radius": 3.5 * mm});
            skCircle(sketch, "E28.2.1.0", {"center": v(-106.9, 616.14) * mm, "radius": 3.5 * mm});
            skCircle(sketch, "E28.2.2.0", {"center": v(-106.9, 591.14) * mm, "radius": 3.5 * mm});
            skCircle(sketch, "E28.2.3.0", {"center": v(-106.9, 566.14) * mm, "radius": 3.5 * mm});
            skCircle(sketch, "E28.2.4.0", {"center": v(-106.9, 541.14) * mm, "radius": 3.5 * mm});
            skCircle(sketch, "E28.2.5.0", {"center": v(-106.9, 516.14) * mm, "radius": 3.5 * mm});
            skCircle(sketch, "E28.2.6.0", {"center": v(-106.9, 491.14) * mm, "radius": 3.5 * mm});
            skCircle(sketch, "E28.2.7.0", {"center": v(-106.9, 466.14) * mm, "radius": 3.5 * mm});
            skCircle(sketch, "E28.2.8.0", {"center": v(-106.9, 441.14) * mm, "radius": 3.5 * mm});
            skCircle(sketch, "E28.2.9.0", {"center": v(-106.9, 416.14) * mm, "radius": 3.5 * mm});
            skCircle(sketch, "E28.2.10.0", {"center": v(-106.9, 391.14) * mm, "radius": 3.5 * mm});
            skCircle(sketch, "E28.3.0.0", {"center": v(-81.9, 641.14) * mm, "radius": 3.5 * mm});
            skCircle(sketch, "E28.3.1.0", {"center": v(-81.9, 616.14) * mm, "radius": 3.5 * mm});
            skCircle(sketch, "E28.3.2.0", {"center": v(-81.9, 591.14) * mm, "radius": 3.5 * mm});
            skCircle(sketch, "E28.3.3.0", {"center": v(-81.9, 566.14) * mm, "radius": 3.5 * mm});
            skCircle(sketch, "E28.3.4.0", {"center": v(-81.9, 541.14) * mm, "radius": 3.5 * mm});
            skCircle(sketch, "E28.3.5.0", {"center": v(-81.9, 516.14) * mm, "radius": 3.5 * mm});
            skCircle(sketch, "E28.3.6.0", {"center": v(-81.9, 491.14) * mm, "radius": 3.5 * mm});
            skCircle(sketch, "E28.3.7.0", {"center": v(-81.9, 466.14) * mm, "radius": 3.5 * mm});
            skCircle(sketch, "E28.3.8.0", {"center": v(-81.9, 441.14) * mm, "radius": 3.5 * mm});
            skCircle(sketch, "E28.3.9.0", {"center": v(-81.9, 416.14) * mm, "radius": 3.5 * mm});
            skCircle(sketch, "E28.3.10.0", {"center": v(-81.9, 391.14) * mm, "radius": 3.5 * mm});
            skCircle(sketch, "E28.4.0.0", {"center": v(-56.9, 641.14) * mm, "radius": 3.5 * mm});
            skCircle(sketch, "E28.4.1.0", {"center": v(-56.9, 616.14) * mm, "radius": 3.5 * mm});
            skCircle(sketch, "E28.4.2.0", {"center": v(-56.9, 591.14) * mm, "radius": 3.5 * mm});
            skCircle(sketch, "E28.4.3.0", {"center": v(-56.9, 566.14) * mm, "radius": 3.5 * mm});
            skCircle(sketch, "E28.4.4.0", {"center": v(-56.9, 541.14) * mm, "radius": 3.5 * mm});
            skCircle(sketch, "E28.4.5.0", {"center": v(-56.9, 516.14) * mm, "radius": 3.5 * mm});
            skCircle(sketch, "E28.4.6.0", {"center": v(-56.9, 491.14) * mm, "radius": 3.5 * mm});
            skCircle(sketch, "E28.4.7.0", {"center": v(-56.9, 466.14) * mm, "radius": 3.5 * mm});
            skCircle(sketch, "E28.4.8.0", {"center": v(-56.9, 441.14) * mm, "radius": 3.5 * mm});
            skCircle(sketch, "E28.4.9.0", {"center": v(-56.9, 416.14) * mm, "radius": 3.5 * mm});
            skCircle(sketch, "E28.4.10.0", {"center": v(-56.9, 391.14) * mm, "radius": 3.5 * mm});
            skCircle(sketch, "E28.5.0.0", {"center": v(-31.9, 641.14) * mm, "radius": 3.5 * mm});
            skCircle(sketch, "E28.5.1.0", {"center": v(-31.9, 616.14) * mm, "radius": 3.5 * mm});
            skCircle(sketch, "E28.5.2.0", {"center": v(-31.9, 591.14) * mm, "radius": 3.5 * mm});
            skCircle(sketch, "E28.5.3.0", {"center": v(-31.9, 566.14) * mm, "radius": 3.5 * mm});
            skCircle(sketch, "E28.5.4.0", {"center": v(-31.9, 541.14) * mm, "radius": 3.5 * mm});
            skCircle(sketch, "E28.5.5.0", {"center": v(-31.9, 516.14) * mm, "radius": 3.5 * mm});
            skCircle(sketch, "E28.5.6.0", {"center": v(-31.9, 491.14) * mm, "radius": 3.5 * mm});
            skCircle(sketch, "E28.5.7.0", {"center": v(-31.9, 466.14) * mm, "radius": 3.5 * mm});
            skCircle(sketch, "E28.5.8.0", {"center": v(-31.9, 441.14) * mm, "radius": 3.5 * mm});
            skCircle(sketch, "E28.5.9.0", {"center": v(-31.9, 416.14) * mm, "radius": 3.5 * mm});
            skCircle(sketch, "E28.5.10.0", {"center": v(-31.9, 391.14) * mm, "radius": 3.5 * mm});
            skCircle(sketch, "E28.6.0.0", {"center": v(-6.9, 641.14) * mm, "radius": 3.5 * mm});
            skCircle(sketch, "E28.6.1.0", {"center": v(-6.9, 616.14) * mm, "radius": 3.5 * mm});
            skCircle(sketch, "E28.6.2.0", {"center": v(-6.9, 591.14) * mm, "radius": 3.5 * mm});
            skCircle(sketch, "E28.6.3.0", {"center": v(-6.9, 566.14) * mm, "radius": 3.5 * mm});
            skCircle(sketch, "E28.6.4.0", {"center": v(-6.9, 541.14) * mm, "radius": 3.5 * mm});
            skCircle(sketch, "E28.6.5.0", {"center": v(-6.9, 516.14) * mm, "radius": 3.5 * mm});
            skCircle(sketch, "E28.6.6.0", {"center": v(-6.9, 491.14) * mm, "radius": 3.5 * mm});
            skCircle(sketch, "E28.6.7.0", {"center": v(-6.9, 466.14) * mm, "radius": 3.5 * mm});
            skCircle(sketch, "E28.6.8.0", {"center": v(-6.9, 441.14) * mm, "radius": 3.5 * mm});
            skCircle(sketch, "E28.6.9.0", {"center": v(-6.9, 416.14) * mm, "radius": 3.5 * mm});
            skCircle(sketch, "E28.6.10.0", {"center": v(-6.9, 391.14) * mm, "radius": 3.5 * mm});
            skCircle(sketch, "E28.7.0.0", {"center": v(18.1, 641.14) * mm, "radius": 3.5 * mm});
            skCircle(sketch, "E28.7.1.0", {"center": v(18.1, 616.14) * mm, "radius": 3.5 * mm});
            skCircle(sketch, "E28.7.2.0", {"center": v(18.1, 591.14) * mm, "radius": 3.5 * mm});
            skCircle(sketch, "E28.7.3.0", {"center": v(18.1, 566.14) * mm, "radius": 3.5 * mm});
            skCircle(sketch, "E28.7.4.0", {"center": v(18.1, 541.14) * mm, "radius": 3.5 * mm});
            skCircle(sketch, "E28.7.5.0", {"center": v(18.1, 516.14) * mm, "radius": 3.5 * mm});
            skCircle(sketch, "E28.7.6.0", {"center": v(18.1, 491.14) * mm, "radius": 3.5 * mm});
            skCircle(sketch, "E28.7.7.0", {"center": v(18.1, 466.14) * mm, "radius": 3.5 * mm});
            skCircle(sketch, "E28.7.8.0", {"center": v(18.1, 441.14) * mm, "radius": 3.5 * mm});
            skCircle(sketch, "E28.7.9.0", {"center": v(18.1, 416.14) * mm, "radius": 3.5 * mm});
            skCircle(sketch, "E28.7.10.0", {"center": v(18.1, 391.14) * mm, "radius": 3.5 * mm});
            skCircle(sketch, "E28.8.0.0", {"center": v(43.1, 641.14) * mm, "radius": 3.5 * mm});
            skCircle(sketch, "E28.8.1.0", {"center": v(43.1, 616.14) * mm, "radius": 3.5 * mm});
            skCircle(sketch, "E28.8.2.0", {"center": v(43.1, 591.14) * mm, "radius": 3.5 * mm});
            skCircle(sketch, "E28.8.3.0", {"center": v(43.1, 566.14) * mm, "radius": 3.5 * mm});
            skCircle(sketch, "E28.8.4.0", {"center": v(43.1, 541.14) * mm, "radius": 3.5 * mm});
            skCircle(sketch, "E28.8.5.0", {"center": v(43.1, 516.14) * mm, "radius": 3.5 * mm});
            skCircle(sketch, "E28.8.6.0", {"center": v(43.1, 491.14) * mm, "radius": 3.5 * mm});
            skCircle(sketch, "E28.8.7.0", {"center": v(43.1, 466.14) * mm, "radius": 3.5 * mm});
            skCircle(sketch, "E28.8.8.0", {"center": v(43.1, 441.14) * mm, "radius": 3.5 * mm});
            skCircle(sketch, "E28.8.9.0", {"center": v(43.1, 416.14) * mm, "radius": 3.5 * mm});
            skCircle(sketch, "E28.8.10.0", {"center": v(43.1, 391.14) * mm, "radius": 3.5 * mm});
            skCircle(sketch, "E28.9.0.0", {"center": v(68.1, 641.14) * mm, "radius": 3.5 * mm});
            skCircle(sketch, "E28.9.1.0", {"center": v(68.1, 616.14) * mm, "radius": 3.5 * mm});
            skCircle(sketch, "E28.9.2.0", {"center": v(68.1, 591.14) * mm, "radius": 3.5 * mm});
            skCircle(sketch, "E28.9.3.0", {"center": v(68.1, 566.14) * mm, "radius": 3.5 * mm});
            skCircle(sketch, "E28.9.4.0", {"center": v(68.1, 541.14) * mm, "radius": 3.5 * mm});
            skCircle(sketch, "E28.9.5.0", {"center": v(68.1, 516.14) * mm, "radius": 3.5 * mm});
            skCircle(sketch, "E28.9.6.0", {"center": v(68.1, 491.14) * mm, "radius": 3.5 * mm});
            skCircle(sketch, "E28.9.7.0", {"center": v(68.1, 466.14) * mm, "radius": 3.5 * mm});
            skCircle(sketch, "E28.9.8.0", {"center": v(68.1, 441.14) * mm, "radius": 3.5 * mm});
            skCircle(sketch, "E28.9.9.0", {"center": v(68.1, 416.14) * mm, "radius": 3.5 * mm});
            skCircle(sketch, "E28.9.10.0", {"center": v(68.1, 391.14) * mm, "radius": 3.5 * mm});
            skCircle(sketch, "E28.10.0.0", {"center": v(93.1, 641.14) * mm, "radius": 3.5 * mm});
            skCircle(sketch, "E28.10.1.0", {"center": v(93.1, 616.14) * mm, "radius": 3.5 * mm});
            skCircle(sketch, "E28.10.2.0", {"center": v(93.1, 591.14) * mm, "radius": 3.5 * mm});
            skCircle(sketch, "E28.10.3.0", {"center": v(93.1, 566.14) * mm, "radius": 3.5 * mm});
            skCircle(sketch, "E28.10.4.0", {"center": v(93.1, 541.14) * mm, "radius": 3.5 * mm});
            skCircle(sketch, "E28.10.5.0", {"center": v(93.1, 516.14) * mm, "radius": 3.5 * mm});
            skCircle(sketch, "E28.10.6.0", {"center": v(93.1, 491.14) * mm, "radius": 3.5 * mm});
            skCircle(sketch, "E28.10.7.0", {"center": v(93.1, 466.14) * mm, "radius": 3.5 * mm});
            skCircle(sketch, "E28.10.8.0", {"center": v(93.1, 441.14) * mm, "radius": 3.5 * mm});
            skCircle(sketch, "E28.10.9.0", {"center": v(93.1, 416.14) * mm, "radius": 3.5 * mm});
            skCircle(sketch, "E28.10.10.0", {"center": v(93.1, 391.14) * mm, "radius": 3.5 * mm});
            skCircle(sketch, "E28.11.0.0", {"center": v(118.1, 641.14) * mm, "radius": 3.5 * mm});
            skCircle(sketch, "E28.11.1.0", {"center": v(118.1, 616.14) * mm, "radius": 3.5 * mm});
            skCircle(sketch, "E28.11.2.0", {"center": v(118.1, 591.14) * mm, "radius": 3.5 * mm});
            skCircle(sketch, "E28.11.3.0", {"center": v(118.1, 566.14) * mm, "radius": 3.5 * mm});
            skCircle(sketch, "E28.11.4.0", {"center": v(118.1, 541.14) * mm, "radius": 3.5 * mm});
            skCircle(sketch, "E28.11.5.0", {"center": v(118.1, 516.14) * mm, "radius": 3.5 * mm});
            skCircle(sketch, "E28.11.6.0", {"center": v(118.1, 491.14) * mm, "radius": 3.5 * mm});
            skCircle(sketch, "E28.11.7.0", {"center": v(118.1, 466.14) * mm, "radius": 3.5 * mm});
            skCircle(sketch, "E28.11.8.0", {"center": v(118.1, 441.14) * mm, "radius": 3.5 * mm});
            skCircle(sketch, "E28.11.9.0", {"center": v(118.1, 416.14) * mm, "radius": 3.5 * mm});
            skCircle(sketch, "E28.11.10.0", {"center": v(118.1, 391.14) * mm, "radius": 3.5 * mm});
            skCircle(sketch, "E28.12.0.0", {"center": v(143.1, 641.14) * mm, "radius": 3.5 * mm});
            skCircle(sketch, "E28.12.1.0", {"center": v(143.1, 616.14) * mm, "radius": 3.5 * mm});
            skCircle(sketch, "E28.12.2.0", {"center": v(143.1, 591.14) * mm, "radius": 3.5 * mm});
            skCircle(sketch, "E28.12.3.0", {"center": v(143.1, 566.14) * mm, "radius": 3.5 * mm});
            skCircle(sketch, "E28.12.4.0", {"center": v(143.1, 541.14) * mm, "radius": 3.5 * mm});
            skCircle(sketch, "E28.12.5.0", {"center": v(143.1, 516.14) * mm, "radius": 3.5 * mm});
            skCircle(sketch, "E28.12.6.0", {"center": v(143.1, 491.14) * mm, "radius": 3.5 * mm});
            skCircle(sketch, "E28.12.7.0", {"center": v(143.1, 466.14) * mm, "radius": 3.5 * mm});
            skCircle(sketch, "E28.12.8.0", {"center": v(143.1, 441.14) * mm, "radius": 3.5 * mm});
            skCircle(sketch, "E28.12.9.0", {"center": v(143.1, 416.14) * mm, "radius": 3.5 * mm});
            skCircle(sketch, "E28.12.10.0", {"center": v(143.1, 391.14) * mm, "radius": 3.5 * mm});
            skCircle(sketch, "E28.13.0.0", {"center": v(168.1, 641.14) * mm, "radius": 3.5 * mm});
            skCircle(sketch, "E28.13.1.0", {"center": v(168.1, 616.14) * mm, "radius": 3.5 * mm});
            skCircle(sketch, "E28.13.2.0", {"center": v(168.1, 591.14) * mm, "radius": 3.5 * mm});
            skCircle(sketch, "E28.13.3.0", {"center": v(168.1, 566.14) * mm, "radius": 3.5 * mm});
            skCircle(sketch, "E28.13.4.0", {"center": v(168.1, 541.14) * mm, "radius": 3.5 * mm});
            skCircle(sketch, "E28.13.5.0", {"center": v(168.1, 516.14) * mm, "radius": 3.5 * mm});
            skCircle(sketch, "E28.13.6.0", {"center": v(168.1, 491.14) * mm, "radius": 3.5 * mm});
            skCircle(sketch, "E28.13.7.0", {"center": v(168.1, 466.14) * mm, "radius": 3.5 * mm});
            skCircle(sketch, "E28.13.8.0", {"center": v(168.1, 441.14) * mm, "radius": 3.5 * mm});
            skCircle(sketch, "E28.13.9.0", {"center": v(168.1, 416.14) * mm, "radius": 3.5 * mm});
            skCircle(sketch, "E28.13.10.0", {"center": v(168.1, 391.14) * mm, "radius": 3.5 * mm});
            skCircle(sketch, "E28.14.0.0", {"center": v(193.1, 641.14) * mm, "radius": 3.5 * mm});
            skCircle(sketch, "E28.14.1.0", {"center": v(193.1, 616.14) * mm, "radius": 3.5 * mm});
            skCircle(sketch, "E28.14.2.0", {"center": v(193.1, 591.14) * mm, "radius": 3.5 * mm});
            skCircle(sketch, "E28.14.3.0", {"center": v(193.1, 566.14) * mm, "radius": 3.5 * mm});
            skCircle(sketch, "E28.14.4.0", {"center": v(193.1, 541.14) * mm, "radius": 3.5 * mm});
            skCircle(sketch, "E28.14.5.0", {"center": v(193.1, 516.14) * mm, "radius": 3.5 * mm});
            skCircle(sketch, "E28.14.6.0", {"center": v(193.1, 491.14) * mm, "radius": 3.5 * mm});
            skCircle(sketch, "E28.14.7.0", {"center": v(193.1, 466.14) * mm, "radius": 3.5 * mm});
            skCircle(sketch, "E28.14.8.0", {"center": v(193.1, 441.14) * mm, "radius": 3.5 * mm});
            skCircle(sketch, "E28.14.9.0", {"center": v(193.1, 416.14) * mm, "radius": 3.5 * mm});
            skCircle(sketch, "E28.14.10.0", {"center": v(193.1, 391.14) * mm, "radius": 3.5 * mm});
            skCircle(sketch, "E28.15.0.0", {"center": v(218.1, 641.14) * mm, "radius": 3.5 * mm});
            skCircle(sketch, "E28.15.1.0", {"center": v(218.1, 616.14) * mm, "radius": 3.5 * mm});
            skCircle(sketch, "E28.15.2.0", {"center": v(218.1, 591.14) * mm, "radius": 3.5 * mm});
            skCircle(sketch, "E28.15.3.0", {"center": v(218.1, 566.14) * mm, "radius": 3.5 * mm});
            skCircle(sketch, "E28.15.4.0", {"center": v(218.1, 541.14) * mm, "radius": 3.5 * mm});
            skCircle(sketch, "E28.15.5.0", {"center": v(218.1, 516.14) * mm, "radius": 3.5 * mm});
            skCircle(sketch, "E28.15.6.0", {"center": v(218.1, 491.14) * mm, "radius": 3.5 * mm});
            skCircle(sketch, "E28.15.7.0", {"center": v(218.1, 466.14) * mm, "radius": 3.5 * mm});
            skCircle(sketch, "E28.15.8.0", {"center": v(218.1, 441.14) * mm, "radius": 3.5 * mm});
            skCircle(sketch, "E28.15.9.0", {"center": v(218.1, 416.14) * mm, "radius": 3.5 * mm});
            skCircle(sketch, "E28.15.10.0", {"center": v(218.1, 391.14) * mm, "radius": 3.5 * mm});
            skCircle(sketch, "E28.16.0.0", {"center": v(243.1, 641.14) * mm, "radius": 3.5 * mm});
            skCircle(sketch, "E28.16.1.0", {"center": v(243.1, 616.14) * mm, "radius": 3.5 * mm});
            skCircle(sketch, "E28.16.2.0", {"center": v(243.1, 591.14) * mm, "radius": 3.5 * mm});
            skCircle(sketch, "E28.16.3.0", {"center": v(243.1, 566.14) * mm, "radius": 3.5 * mm});
            skCircle(sketch, "E28.16.4.0", {"center": v(243.1, 541.14) * mm, "radius": 3.5 * mm});
            skCircle(sketch, "E28.16.5.0", {"center": v(243.1, 516.14) * mm, "radius": 3.5 * mm});
            skCircle(sketch, "E28.16.6.0", {"center": v(243.1, 491.14) * mm, "radius": 3.5 * mm});
            skCircle(sketch, "E28.16.7.0", {"center": v(243.1, 466.14) * mm, "radius": 3.5 * mm});
            skCircle(sketch, "E28.16.8.0", {"center": v(243.1, 441.14) * mm, "radius": 3.5 * mm});
            skCircle(sketch, "E28.16.9.0", {"center": v(243.1, 416.14) * mm, "radius": 3.5 * mm});
            skCircle(sketch, "E28.16.10.0", {"center": v(243.1, 391.14) * mm, "radius": 3.5 * mm});
            skCircle(sketch, "E28.17.0.0", {"center": v(268.1, 641.14) * mm, "radius": 3.5 * mm});
            skCircle(sketch, "E28.17.1.0", {"center": v(268.1, 616.14) * mm, "radius": 3.5 * mm});
            skCircle(sketch, "E28.17.2.0", {"center": v(268.1, 591.14) * mm, "radius": 3.5 * mm});
            skCircle(sketch, "E28.17.3.0", {"center": v(268.1, 566.14) * mm, "radius": 3.5 * mm});
            skCircle(sketch, "E28.17.4.0", {"center": v(268.1, 541.14) * mm, "radius": 3.5 * mm});
            skCircle(sketch, "E28.17.5.0", {"center": v(268.1, 516.14) * mm, "radius": 3.5 * mm});
            skCircle(sketch, "E28.17.6.0", {"center": v(268.1, 491.14) * mm, "radius": 3.5 * mm});
            skCircle(sketch, "E28.17.7.0", {"center": v(268.1, 466.14) * mm, "radius": 3.5 * mm});
            skCircle(sketch, "E28.17.8.0", {"center": v(268.1, 441.14) * mm, "radius": 3.5 * mm});
            skCircle(sketch, "E28.17.9.0", {"center": v(268.1, 416.14) * mm, "radius": 3.5 * mm});
            skCircle(sketch, "E28.17.10.0", {"center": v(268.1, 391.14) * mm, "radius": 3.5 * mm});
            skCircle(sketch, "E28.18.0.0", {"center": v(293.1, 641.14) * mm, "radius": 3.5 * mm});
            skCircle(sketch, "E28.18.1.0", {"center": v(293.1, 616.14) * mm, "radius": 3.5 * mm});
            skCircle(sketch, "E28.18.2.0", {"center": v(293.1, 591.14) * mm, "radius": 3.5 * mm});
            skCircle(sketch, "E28.18.3.0", {"center": v(293.1, 566.14) * mm, "radius": 3.5 * mm});
            skCircle(sketch, "E28.18.4.0", {"center": v(293.1, 541.14) * mm, "radius": 3.5 * mm});
            skCircle(sketch, "E28.18.5.0", {"center": v(293.1, 516.14) * mm, "radius": 3.5 * mm});
            skCircle(sketch, "E28.18.6.0", {"center": v(293.1, 491.14) * mm, "radius": 3.5 * mm});
            skCircle(sketch, "E28.18.7.0", {"center": v(293.1, 466.14) * mm, "radius": 3.5 * mm});
            skCircle(sketch, "E28.18.8.0", {"center": v(293.1, 441.14) * mm, "radius": 3.5 * mm});
            skCircle(sketch, "E28.18.9.0", {"center": v(293.1, 416.14) * mm, "radius": 3.5 * mm});
            skCircle(sketch, "E28.18.10.0", {"center": v(293.1, 391.14) * mm, "radius": 3.5 * mm});
            skCircle(sketch, "E28.19.0.0", {"center": v(318.1, 641.14) * mm, "radius": 3.5 * mm});
            skCircle(sketch, "E28.19.1.0", {"center": v(318.1, 616.14) * mm, "radius": 3.5 * mm});
            skCircle(sketch, "E28.19.2.0", {"center": v(318.1, 591.14) * mm, "radius": 3.5 * mm});
            skCircle(sketch, "E28.19.3.0", {"center": v(318.1, 566.14) * mm, "radius": 3.5 * mm});
            skCircle(sketch, "E28.19.4.0", {"center": v(318.1, 541.14) * mm, "radius": 3.5 * mm});
            skCircle(sketch, "E28.19.5.0", {"center": v(318.1, 516.14) * mm, "radius": 3.5 * mm});
            skCircle(sketch, "E28.19.6.0", {"center": v(318.1, 491.14) * mm, "radius": 3.5 * mm});
            skCircle(sketch, "E28.19.7.0", {"center": v(318.1, 466.14) * mm, "radius": 3.5 * mm});
            skCircle(sketch, "E28.19.8.0", {"center": v(318.1, 441.14) * mm, "radius": 3.5 * mm});
            skCircle(sketch, "E28.19.9.0", {"center": v(318.1, 416.14) * mm, "radius": 3.5 * mm});
            skCircle(sketch, "E28.19.10.0", {"center": v(318.1, 391.14) * mm, "radius": 3.5 * mm});
            skCircle(sketch, "E28.20.0.0", {"center": v(343.1, 641.14) * mm, "radius": 3.5 * mm});
            skCircle(sketch, "E28.20.1.0", {"center": v(343.1, 616.14) * mm, "radius": 3.5 * mm});
            skCircle(sketch, "E28.20.2.0", {"center": v(343.1, 591.14) * mm, "radius": 3.5 * mm});
            skCircle(sketch, "E28.20.3.0", {"center": v(343.1, 566.14) * mm, "radius": 3.5 * mm});
            skCircle(sketch, "E28.20.4.0", {"center": v(343.1, 541.14) * mm, "radius": 3.5 * mm});
            skCircle(sketch, "E28.20.5.0", {"center": v(343.1, 516.14) * mm, "radius": 3.5 * mm});
            skCircle(sketch, "E28.20.6.0", {"center": v(343.1, 491.14) * mm, "radius": 3.5 * mm});
            skCircle(sketch, "E28.20.7.0", {"center": v(343.1, 466.14) * mm, "radius": 3.5 * mm});
            skCircle(sketch, "E28.20.8.0", {"center": v(343.1, 441.14) * mm, "radius": 3.5 * mm});
            skCircle(sketch, "E28.20.9.0", {"center": v(343.1, 416.14) * mm, "radius": 3.5 * mm});
            skCircle(sketch, "E28.20.10.0", {"center": v(343.1, 391.14) * mm, "radius": 3.5 * mm});
            skCircle(sketch, "E28.21.0.0", {"center": v(368.1, 641.14) * mm, "radius": 3.5 * mm});
            skCircle(sketch, "E28.21.1.0", {"center": v(368.1, 616.14) * mm, "radius": 3.5 * mm});
            skCircle(sketch, "E28.21.2.0", {"center": v(368.1, 591.14) * mm, "radius": 3.5 * mm});
            skCircle(sketch, "E28.21.3.0", {"center": v(368.1, 566.14) * mm, "radius": 3.5 * mm});
            skCircle(sketch, "E28.21.4.0", {"center": v(368.1, 541.14) * mm, "radius": 3.5 * mm});
            skCircle(sketch, "E28.21.5.0", {"center": v(368.1, 516.14) * mm, "radius": 3.5 * mm});
            skCircle(sketch, "E28.21.6.0", {"center": v(368.1, 491.14) * mm, "radius": 3.5 * mm});
            skCircle(sketch, "E28.21.7.0", {"center": v(368.1, 466.14) * mm, "radius": 3.5 * mm});
            skCircle(sketch, "E28.21.8.0", {"center": v(368.1, 441.14) * mm, "radius": 3.5 * mm});
            skCircle(sketch, "E28.21.9.0", {"center": v(368.1, 416.14) * mm, "radius": 3.5 * mm});
            skCircle(sketch, "E28.21.10.0", {"center": v(368.1, 391.14) * mm, "radius": 3.5 * mm});
            skCircle(sketch, "E28.22.0.0", {"center": v(393.1, 641.14) * mm, "radius": 3.5 * mm});
            skCircle(sketch, "E28.22.1.0", {"center": v(393.1, 616.14) * mm, "radius": 3.5 * mm});
            skCircle(sketch, "E28.22.2.0", {"center": v(393.1, 591.14) * mm, "radius": 3.5 * mm});
            skCircle(sketch, "E28.22.3.0", {"center": v(393.1, 566.14) * mm, "radius": 3.5 * mm});
            skCircle(sketch, "E28.22.4.0", {"center": v(393.1, 541.14) * mm, "radius": 3.5 * mm});
            skCircle(sketch, "E28.22.5.0", {"center": v(393.1, 516.14) * mm, "radius": 3.5 * mm});
            skCircle(sketch, "E28.22.6.0", {"center": v(393.1, 491.14) * mm, "radius": 3.5 * mm});
            skCircle(sketch, "E28.22.7.0", {"center": v(393.1, 466.14) * mm, "radius": 3.5 * mm});
            skCircle(sketch, "E28.22.8.0", {"center": v(393.1, 441.14) * mm, "radius": 3.5 * mm});
            skCircle(sketch, "E28.22.9.0", {"center": v(393.1, 416.14) * mm, "radius": 3.5 * mm});
            skCircle(sketch, "E28.22.10.0", {"center": v(393.1, 391.14) * mm, "radius": 3.5 * mm});
            skLineSegment(sketch, "E28.direction1", {"start": v(-156.9, 641.14) * mm, "end": v(-131.9, 641.14) * mm, "construction": true});
            skLineSegment(sketch, "E28.direction2", {"start": v(-156.9, 641.14) * mm, "end": v(-156.9, 616.14) * mm, "construction": true});
            skCircle(sketch, "E29.0.23.0", {"center": v(418.1, 641.14) * mm, "radius": 3.5 * mm});
            skCircle(sketch, "E29.0.23.1", {"center": v(418.1, 616.14) * mm, "radius": 3.5 * mm});
            skCircle(sketch, "E29.0.23.2", {"center": v(418.1, 591.14) * mm, "radius": 3.5 * mm});
            skCircle(sketch, "E29.0.23.3", {"center": v(418.1, 566.14) * mm, "radius": 3.5 * mm});
            skCircle(sketch, "E29.0.23.4", {"center": v(418.1, 541.14) * mm, "radius": 3.5 * mm});
            skCircle(sketch, "E29.0.23.5", {"center": v(418.1, 516.14) * mm, "radius": 3.5 * mm});
            skCircle(sketch, "E29.0.23.6", {"center": v(418.1, 491.14) * mm, "radius": 3.5 * mm});
            skCircle(sketch, "E29.0.23.7", {"center": v(418.1, 466.14) * mm, "radius": 3.5 * mm});
            skCircle(sketch, "E29.0.23.8", {"center": v(418.1, 441.14) * mm, "radius": 3.5 * mm});
            skCircle(sketch, "E29.0.23.9", {"center": v(418.1, 416.14) * mm, "radius": 3.5 * mm});
            skCircle(sketch, "E29.0.23.10", {"center": v(418.1, 391.14) * mm, "radius": 3.5 * mm});
            skSolve(sketch);
        }
        {
            var Q0;
            Q0=qSketchRegion(id+"F24",true);
            extrude(context, id + "F25", {"entities" : qUnion([Q0]), "depth" : 6 * mm, "offsetDistance" : 25 * mm});
        }
    });
